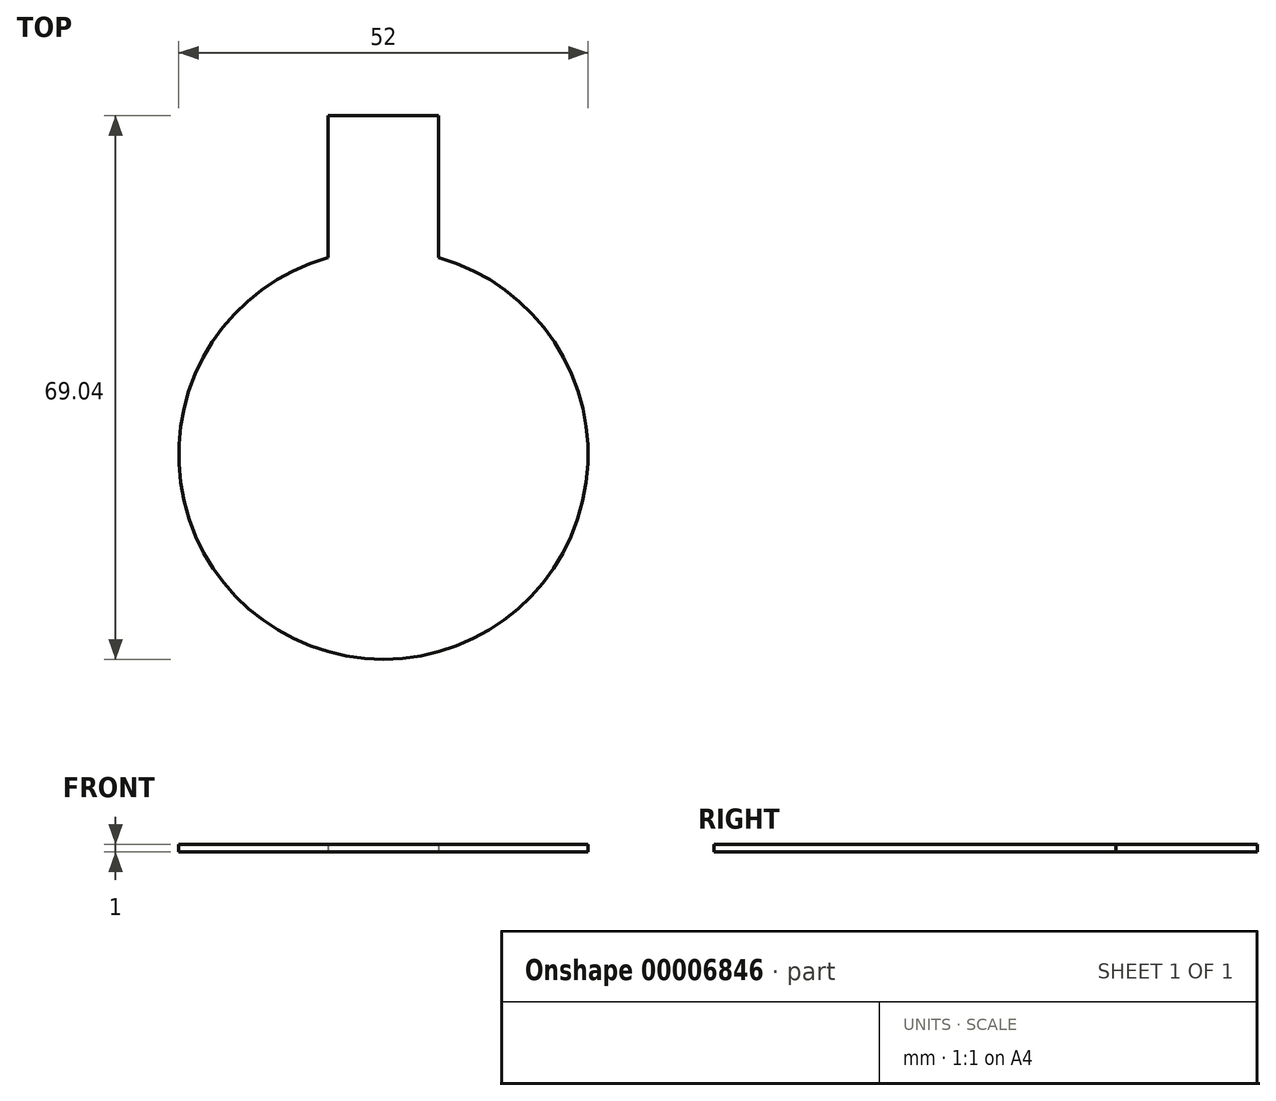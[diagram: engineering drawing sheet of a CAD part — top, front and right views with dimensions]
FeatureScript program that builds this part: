
annotation { "Feature Type Name" : "Feature", "Feature Type Description" : "" }
export const myFeature = defineFeature(function(context is Context, id is Id, definition is map)
    precondition{}
    {
        {
            var Q0;
            Q0=qCreatedBy(makeId("Top.planeOp"),FACE);
            var sketch = newSketch(context, id + "F0", { "sketchPlane" : qUnion([Q0])});
            skArc(sketch, "E0", {"start": v(-7, 25.04) * mm, "mid": v(0, -26) * mm, "end": v(7, 25.04) * mm});
            skLineSegment(sketch, "E1", {"start": v(-7, 43.04) * mm, "end": v(7, 43.04) * mm});
            skPoint(sketch, "E2", {"position": v(0, 43.04) * mm});
            skLineSegment(sketch, "E3", {"start": v(7, 43.04) * mm, "end": v(7, 25.04) * mm});
            skLineSegment(sketch, "E4", {"start": v(-7, 43.04) * mm, "end": v(-7, 25.04) * mm});
            skSolve(sketch);
        }
        {
            var Q0;
            Q0=makeQuery(id+"F0.imprint","IMPRINT",FACE,{"disambiguationData":[TD([[makeQuery(id+"F0.imprint","IMPRINT",EDGE,{"derivedFrom":sQuery(id+"F0.wireOp",EDGE,"E0")}),1.0]])]});
            extrude(context, id + "F1", {"entities" : qUnion([Q0]), "depth" : 1 * mm});
        }
    });
